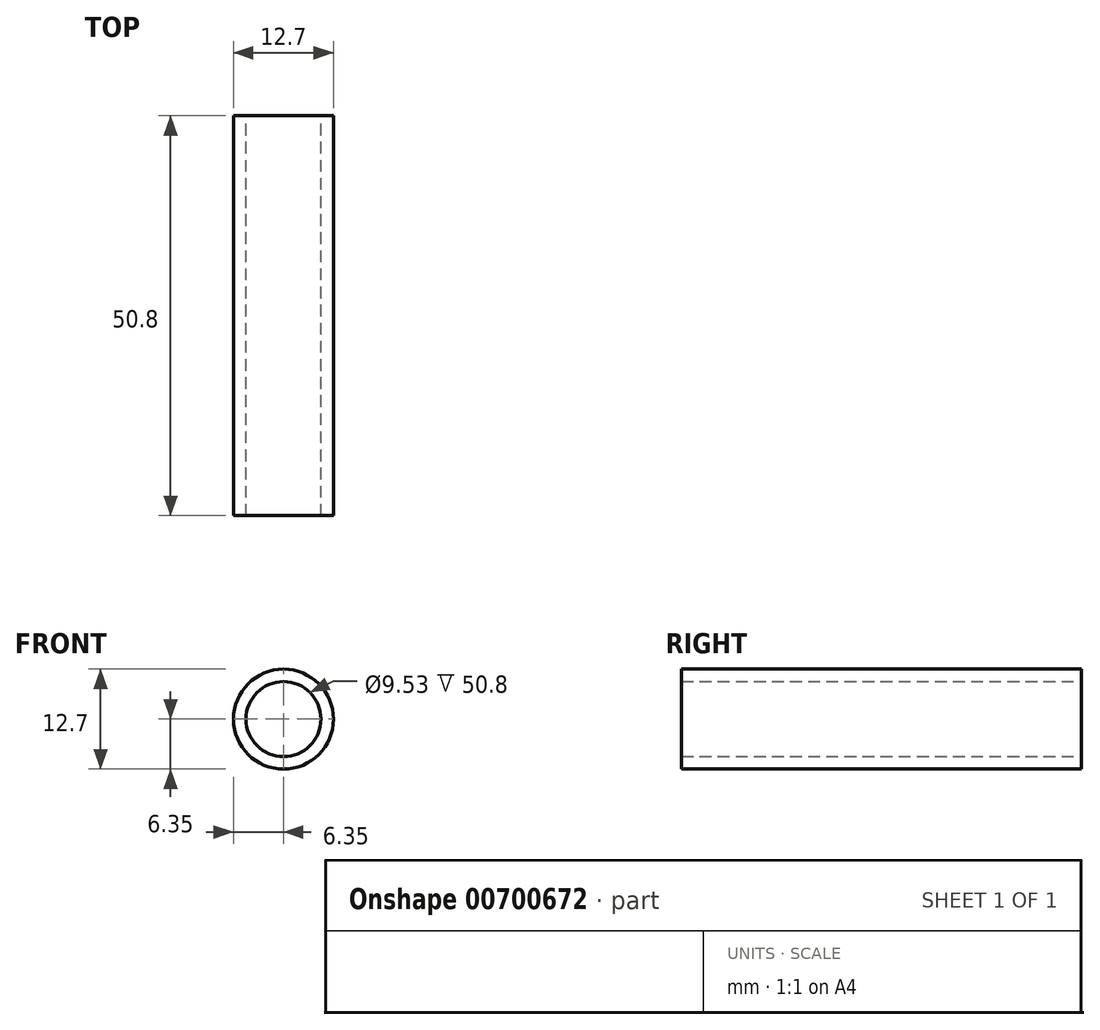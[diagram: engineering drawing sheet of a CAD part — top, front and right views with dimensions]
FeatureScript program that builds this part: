
annotation { "Feature Type Name" : "Feature", "Feature Type Description" : "" }
export const myFeature = defineFeature(function(context is Context, id is Id, definition is map)
    precondition{}
    {
        {
            var Q0;
            Q0=qCreatedBy(makeId("Front.planeOp"),FACE);
            var sketch = newSketch(context, id + "F0", { "sketchPlane" : qUnion([Q0])});
            skCircle(sketch, "E0", {"center": v(0, 0) * mm, "radius": 4.76 * mm});
            skCircle(sketch, "E1", {"center": v(0, 0) * mm, "radius": 6.35 * mm});
            skSolve(sketch);
        }
        {
            var Q0;
            Q0 = qSketchRegion(id + "F0", true);
            extrude(context, id + "F1", {"entities" : qUnion([Q0]), "depth" : 50.8 * mm, "offsetDistance" : 25.4 * mm});
        }
    });
